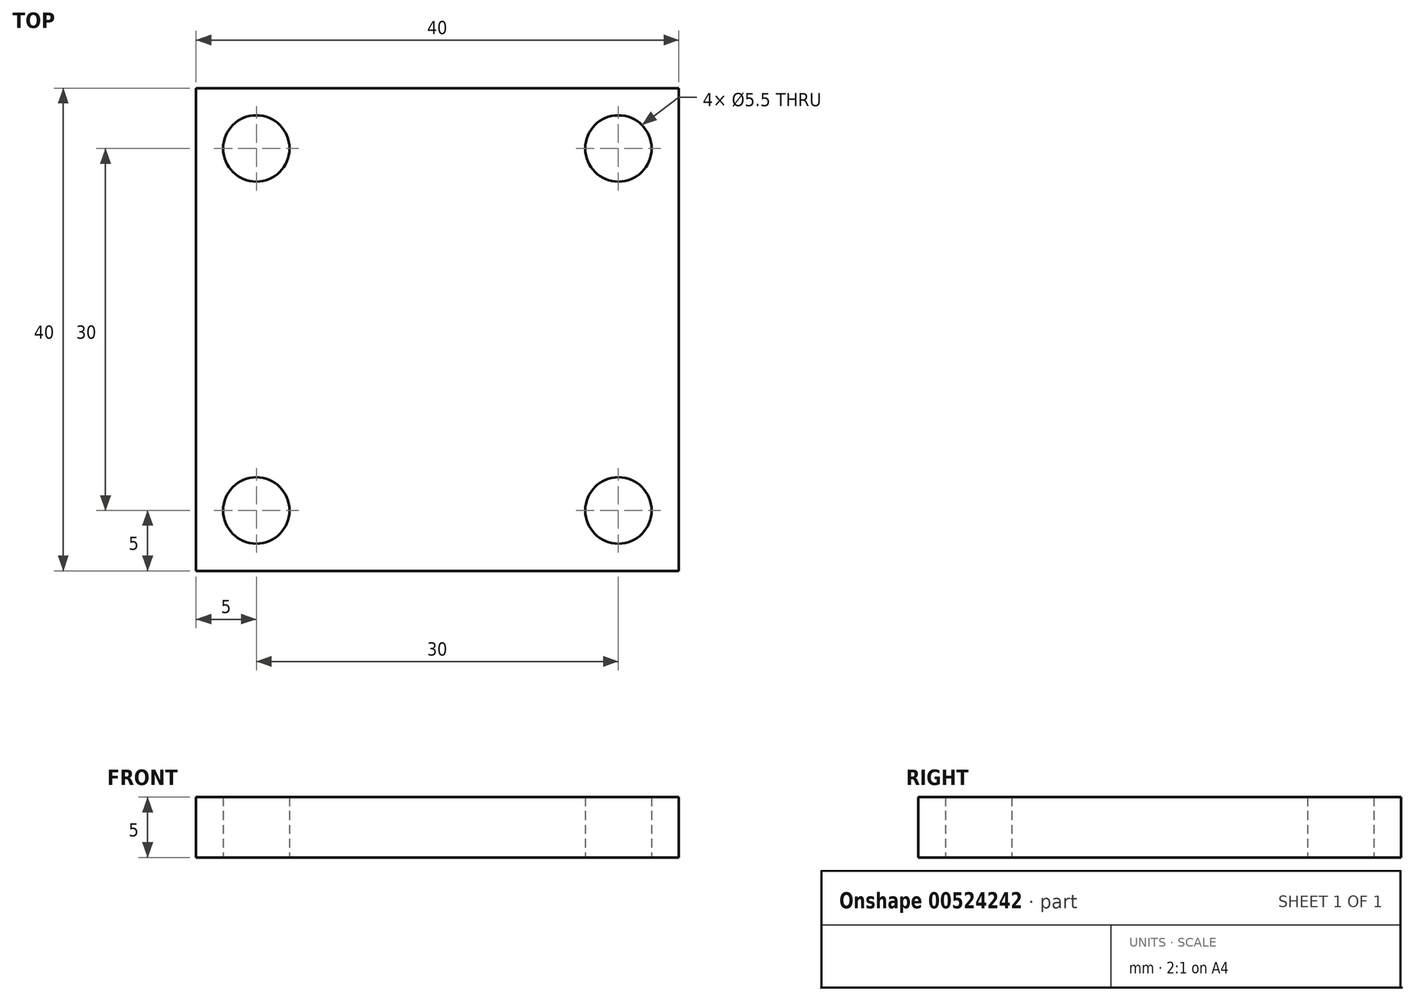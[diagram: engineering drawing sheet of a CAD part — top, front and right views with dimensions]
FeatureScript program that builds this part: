
annotation { "Feature Type Name" : "Feature", "Feature Type Description" : "" }
export const myFeature = defineFeature(function(context is Context, id is Id, definition is map)
    precondition{}
    {
        {
            var Q0;
            Q0=qCreatedBy(makeId("Top.planeOp"),FACE);
            var sketch = newSketch(context, id + "F0", { "sketchPlane" : qUnion([Q0])});
            skLineSegment(sketch, "E0.bottom", {"start": v(0, 0) * mm, "end": v(40, 0) * mm});
            skLineSegment(sketch, "E0.top", {"start": v(0, -40) * mm, "end": v(40, -40) * mm});
            skLineSegment(sketch, "E0.left", {"start": v(0, 0) * mm, "end": v(0, -40) * mm});
            skLineSegment(sketch, "E0.right", {"start": v(40, 0) * mm, "end": v(40, -40) * mm});
            skPoint(sketch, "E1", {"position": v(5, -5) * mm});
            skPoint(sketch, "E2", {"position": v(35, -5) * mm});
            skPoint(sketch, "E3", {"position": v(5, -35) * mm});
            skPoint(sketch, "E4", {"position": v(35, -35) * mm});
            skSolve(sketch);
        }
        {
            var Q0;
            Q0=makeQuery(id+"F0.imprint","IMPRINT",FACE,{"disambiguationData":[TD([[makeQuery(id+"F0.imprint","IMPRINT",EDGE,{"derivedFrom":sQuery(id+"F0.wireOp",EDGE,"E0.bottom")}),-1.0]])]});
            extrude(context, id + "F1", {"entities" : qUnion([Q0]), "depth" : 5 * mm, "offsetDistance" : 25 * mm});
        }
        {
            var Q0;
            Q0=sQuery(id+"F0.wireOp",VERTEX,"E1");
            var Q1;
            Q1=sQuery(id+"F0.wireOp",VERTEX,"E3");
            var Q2;
            Q2=sQuery(id+"F0.wireOp",VERTEX,"E4");
            var Q3;
            Q3=sQuery(id+"F0.wireOp",VERTEX,"E2");
            var Q4;
            Q4=makeQuery(id+"F1.opExtrude","SWEPT_BODY",BODY,{"disambiguationData":[OSD([sQuery(id+"F0.wireOp",EDGE,"E0.bottom"),sQuery(id+"F0.wireOp",EDGE,"E0.top"),sQuery(id+"F0.wireOp",EDGE,"E0.left"),sQuery(id+"F0.wireOp",EDGE,"E0.right")])]});
            hole(context, id + "F2", {"style" : HoleStyle.SIMPLE, "endStyle" : HoleEndStyle.THROUGH, "oppositeDirection" : true, "standardTappedOrClearance" : lookupTablePath({ "standard" : "ISO", "fit" : "Normal", "size" : "M5", "type" : "Clearance" }), "standardBlindInLast" : lookupTablePath({ "fit" : "Standard", "standard" : "ISO", "size" : "M5", "type" : "Clearance" }), "holeDiameter" : 5.5 * mm, "isTappedThrough" : true, "tappedDepth" : 12 * mm, "tapClearance" : 3, "locations" : qUnion([Q0, Q1, Q2, Q3]), "scope" : qUnion([Q4])});
        }
    });
